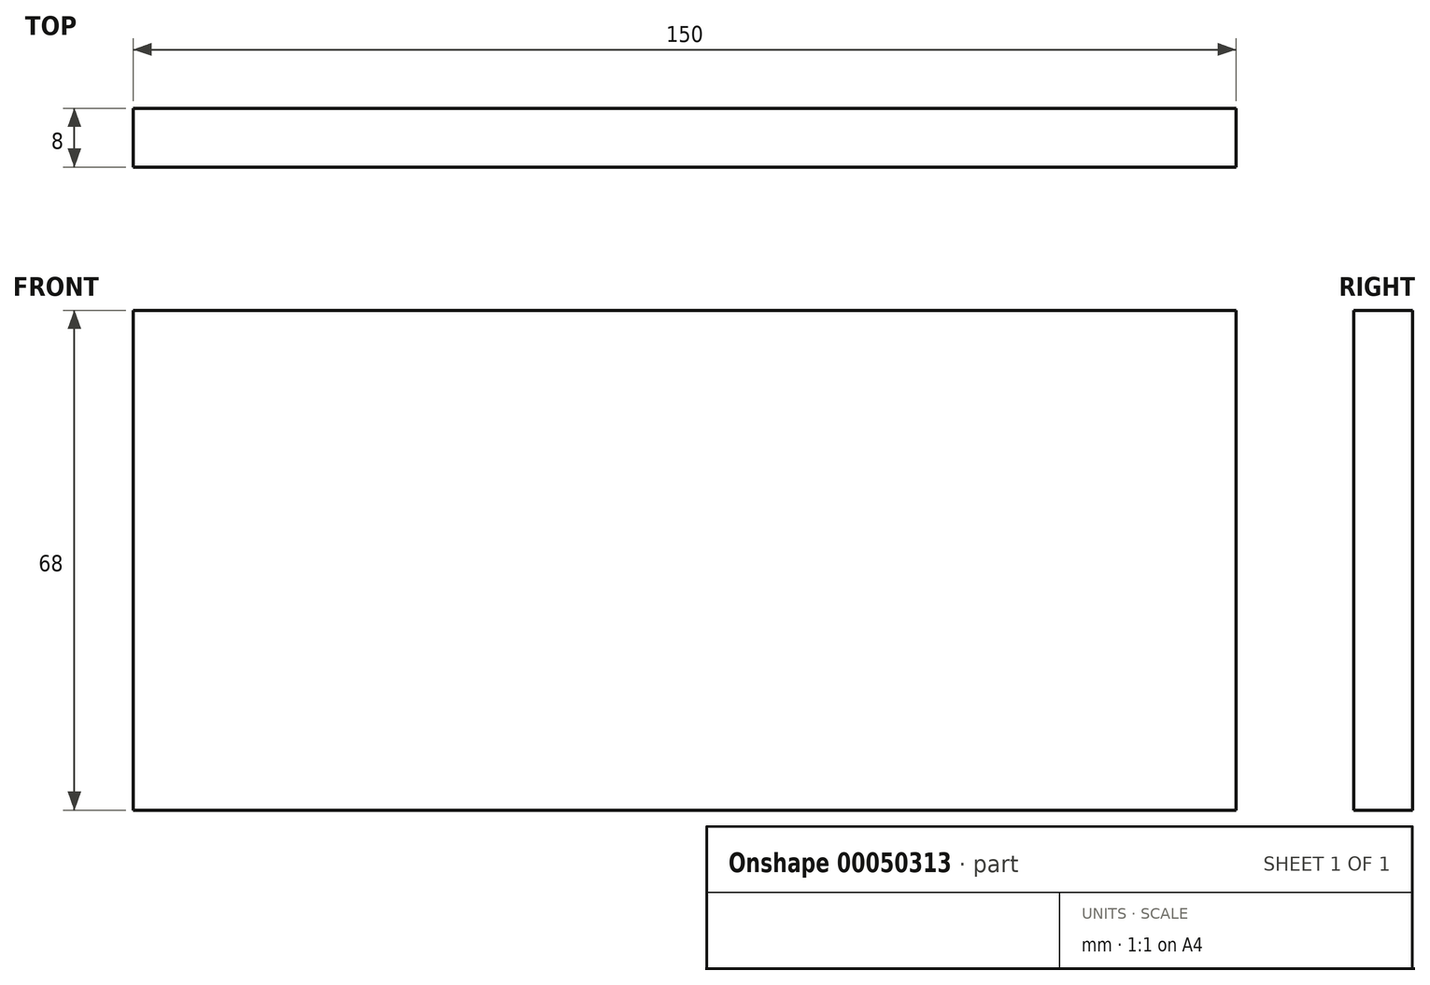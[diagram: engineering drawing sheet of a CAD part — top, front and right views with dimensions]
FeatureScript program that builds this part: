
annotation { "Feature Type Name" : "Feature", "Feature Type Description" : "" }
export const myFeature = defineFeature(function(context is Context, id is Id, definition is map)
    precondition{}
    {
        {
            var Q0;
            Q0=qCreatedBy(makeId("Front.planeOp"),FACE);
            var sketch = newSketch(context, id + "F0", { "sketchPlane" : qUnion([Q0])});
            skLineSegment(sketch, "E0.bottom", {"start": v(0, 0) * mm, "end": v(-150, 0) * mm});
            skLineSegment(sketch, "E0.top", {"start": v(0, -68) * mm, "end": v(-150, -68) * mm});
            skLineSegment(sketch, "E0.left", {"start": v(0, 0) * mm, "end": v(0, -68) * mm});
            skLineSegment(sketch, "E0.right", {"start": v(-150, 0) * mm, "end": v(-150, -68) * mm});
            skSolve(sketch);
        }
        {
            var Q0;
            Q0=qSketchRegion(id+"F0",true);
            extrude(context, id + "F1", {"entities" : qUnion([Q0]), "depth" : 8 * mm});
        }
    });
